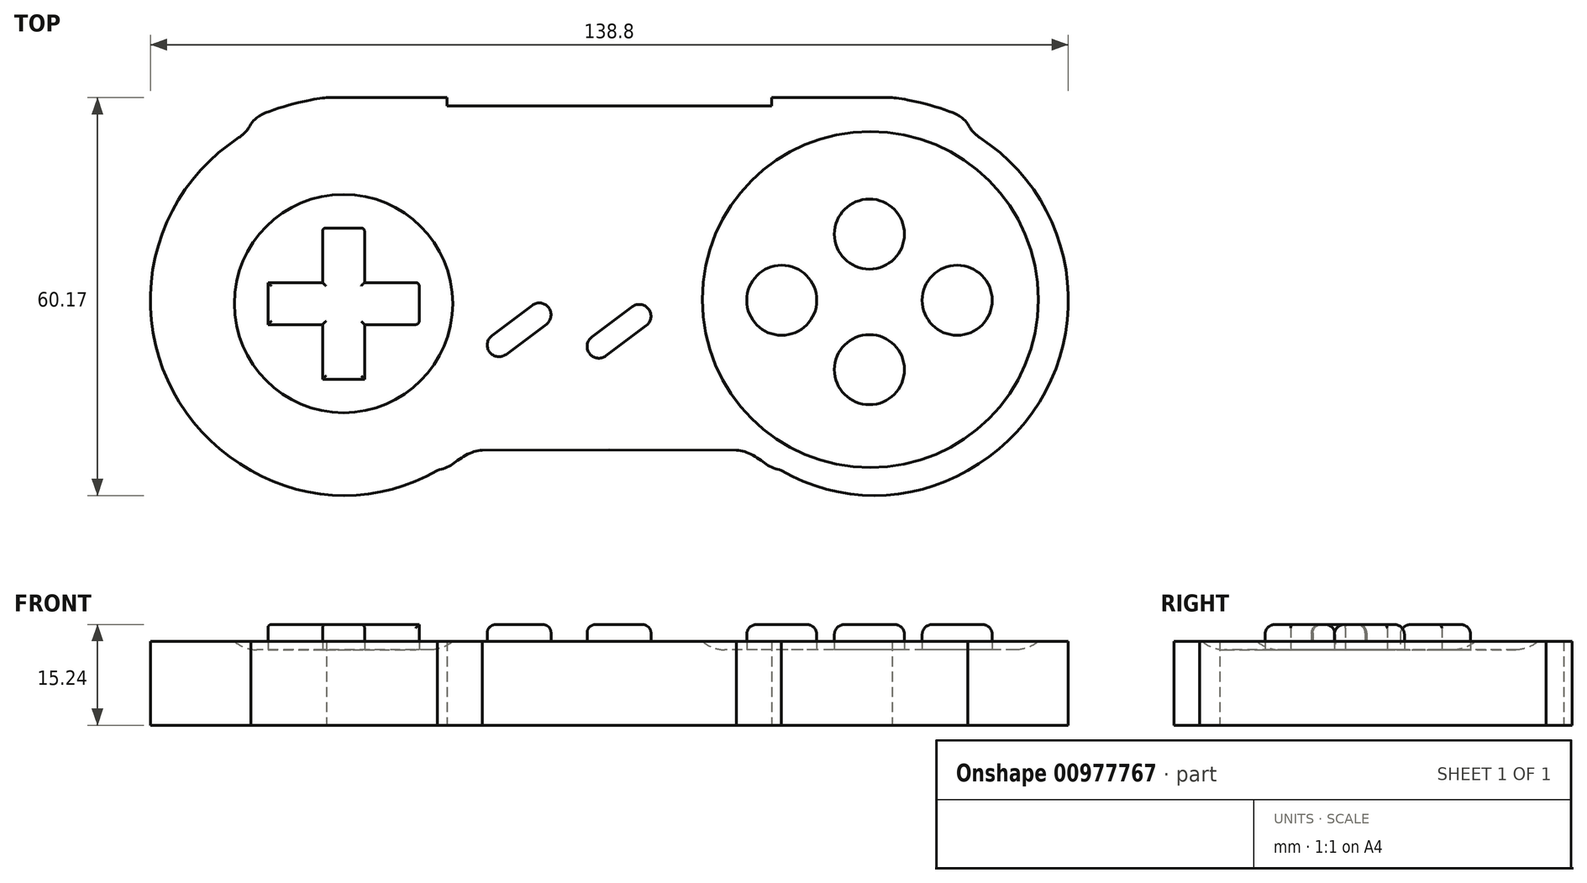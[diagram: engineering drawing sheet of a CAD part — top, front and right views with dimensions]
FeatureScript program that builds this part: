
annotation { "Feature Type Name" : "Feature", "Feature Type Description" : "" }
export const myFeature = defineFeature(function(context is Context, id is Id, definition is map)
    precondition{}
    {
        {
            var Q0;
            Q0=qCreatedBy(makeId("Top.planeOp"),FACE);
            var sketch = newSketch(context, id + "F0", { "sketchPlane" : qUnion([Q0])});
            skLineSegment(sketch, "E0.top", {"start": v(72.48, 34.93) * mm, "end": v(-72.48, 34.93) * mm});
            skLineSegment(sketch, "E0.left", {"start": v(72.48, -34.93) * mm, "end": v(72.48, 34.93) * mm});
            skLineSegment(sketch, "E0.right", {"start": v(-72.48, -34.93) * mm, "end": v(-72.48, 34.93) * mm});
            skPoint(sketch, "E0.middle", {"position": v(0, 0) * mm});
            skLineSegment(sketch, "E1", {"start": v(-72.48, -34.93) * mm, "end": v(72.48, -34.93) * mm});
            skLineSegment(sketch, "E2", {"start": v(0, 0) * mm, "end": v(0, 26.38) * mm});
            skLineSegment(sketch, "E3", {"start": v(0, 0) * mm, "end": v(0, -25.63) * mm});
            skLineSegment(sketch, "E4", {"start": v(0, 26.38) * mm, "end": v(-24.55, 26.38) * mm});
            skLineSegment(sketch, "E5", {"start": v(-24.55, 26.38) * mm, "end": v(-24.55, 27.65) * mm});
            skLineSegment(sketch, "E6", {"start": v(-24.55, 27.65) * mm, "end": v(-42.75, 27.65) * mm});
            skLineSegment(sketch, "E7", {"start": v(-54.18, 23.7) * mm, "end": v(-54.18, 22.7) * mm});
            skFitSpline(sketch, "E8", {"points": [v(-42.75, 27.65) * mm, v(-45.46, 27.23) * mm, v(-52.7, 25) * mm, v(-54.18, 23.7) * mm], "startDerivative": vector(-7.67, -0.85) * mm, "endDerivative": vector(-4.06, -5.33) * mm});
            skArc(sketch, "E9", {"start": v(-54.18, 22.7) * mm, "mid": v(-69.4, -3) * mm, "end": v(-54.18, -28.7) * mm});
            skArc(sketch, "E10", {"start": v(-54.18, -28.7) * mm, "mid": v(-40.08, -32.52) * mm, "end": v(-25.98, -28.7) * mm});
            skFitSpline(sketch, "E11", {"points": [v(-25.98, -28.7) * mm, v(-24.4, -28.18) * mm, v(-22.93, -27.2) * mm, v(-20.95, -26.07) * mm, v(-19.23, -25.65) * mm], "startDerivative": vector(6.95, 1.75) * mm, "endDerivative": vector(6.95, 1.14) * mm});
            skLineSegment(sketch, "E12", {"start": v(-19.23, -25.65) * mm, "end": v(0, -25.63) * mm});
            skLineSegment(sketch, "E13.MirrorCS", {"start": v(19.23, -25.65) * mm, "end": v(0, -25.63) * mm});
            skFitSpline(sketch, "E14.MirrorCS", {"points": [v(25.98, -28.7) * mm, v(24.4, -28.18) * mm, v(22.93, -27.2) * mm, v(20.95, -26.07) * mm, v(19.23, -25.65) * mm], "startDerivative": vector(-6.95, 1.75) * mm, "endDerivative": vector(-6.95, 1.14) * mm});
            skLineSegment(sketch, "E15.MirrorCS", {"start": v(0, 26.38) * mm, "end": v(24.55, 26.38) * mm});
            skLineSegment(sketch, "E16.MirrorCS", {"start": v(24.55, 27.65) * mm, "end": v(42.75, 27.65) * mm});
            skLineSegment(sketch, "E17.MirrorCS", {"start": v(24.55, 26.38) * mm, "end": v(24.55, 27.65) * mm});
            skFitSpline(sketch, "E18.MirrorCS", {"points": [v(42.75, 27.65) * mm, v(45.46, 27.23) * mm, v(52.7, 25) * mm, v(54.18, 23.7) * mm], "startDerivative": vector(7.67, -0.85) * mm, "endDerivative": vector(4.06, -5.33) * mm});
            skArc(sketch, "E19.MirrorCS", {"start": v(54.18, 22.7) * mm, "mid": v(69.4, -3) * mm, "end": v(54.18, -28.7) * mm});
            skLineSegment(sketch, "E20.MirrorCS", {"start": v(54.18, 23.7) * mm, "end": v(54.18, 22.7) * mm});
            skArc(sketch, "E21.MirrorCS", {"start": v(54.18, -28.7) * mm, "mid": v(40.08, -32.52) * mm, "end": v(25.98, -28.7) * mm});
            skSolve(sketch);
        }
        {
            var Q0;
            Q0=makeQuery(id+"F0.imprint","IMPRINT",FACE,{"disambiguationData":[TD([[makeQuery(id+"F0.imprint","IMPRINT",EDGE,{"derivedFrom":sQuery(id+"F0.wireOp",EDGE,"E2")}),1.0]])]});
            var Q1;
            Q1=makeQuery(id+"F0.imprint","IMPRINT",FACE,{"disambiguationData":[TD([[makeQuery(id+"F0.imprint","IMPRINT",EDGE,{"derivedFrom":sQuery(id+"F0.wireOp",EDGE,"E2")}),-1.0]])]});
            extrude(context, id + "F1", {"entities" : qUnion([Q0, Q1]), "depth" : 12.7 * mm, "offsetDistance" : 25.4 * mm});
        }
        {
            var Q0;
            Q0=makeQuery(id+"F1.opExtrude","CAP_FACE",FACE,{"disambiguationData":[OSD([sQuery(id+"F0.wireOp",EDGE,"E4"),sQuery(id+"F0.wireOp",EDGE,"E5"),sQuery(id+"F0.wireOp",EDGE,"E6"),sQuery(id+"F0.wireOp",EDGE,"E7"),sQuery(id+"F0.wireOp",EDGE,"E8"),sQuery(id+"F0.wireOp",EDGE,"E9"),sQuery(id+"F0.wireOp",EDGE,"E10"),sQuery(id+"F0.wireOp",EDGE,"E11"),sQuery(id+"F0.wireOp",EDGE,"E12"),sQuery(id+"F0.wireOp",EDGE,"E13.MirrorCS"),sQuery(id+"F0.wireOp",EDGE,"E14.MirrorCS"),sQuery(id+"F0.wireOp",EDGE,"E15.MirrorCS"),sQuery(id+"F0.wireOp",EDGE,"E16.MirrorCS"),sQuery(id+"F0.wireOp",EDGE,"E17.MirrorCS"),sQuery(id+"F0.wireOp",EDGE,"E18.MirrorCS"),sQuery(id+"F0.wireOp",EDGE,"E19.MirrorCS"),sQuery(id+"F0.wireOp",EDGE,"E20.MirrorCS"),sQuery(id+"F0.wireOp",EDGE,"E21.MirrorCS")])],"isStart":false});
            var sketch = newSketch(context, id + "F2", { "sketchPlane" : qUnion([Q0])});
            skLineSegment(sketch, "E22", {"start": v(-51.62, -3.49) * mm, "end": v(-51.62, -0.31) * mm});
            skLineSegment(sketch, "E23", {"start": v(-28.76, -3.49) * mm, "end": v(-28.76, -6.66) * mm});
            skLineSegment(sketch, "E24", {"start": v(-40.19, 7.94) * mm, "end": v(-43.36, 7.94) * mm});
            skLineSegment(sketch, "E25", {"start": v(-40.19, -14.92) * mm, "end": v(-37.01, -14.92) * mm});
            skLineSegment(sketch, "E26.bottom", {"start": v(-51.62, -0.31) * mm, "end": v(-43.36, -0.31) * mm});
            skLineSegment(sketch, "E26.top", {"start": v(-51.62, -6.66) * mm, "end": v(-43.36, -6.66) * mm});
            skLineSegment(sketch, "E26.left", {"start": v(-51.62, -0.31) * mm, "end": v(-51.62, -6.66) * mm});
            skLineSegment(sketch, "E26.right", {"start": v(-28.76, -0.31) * mm, "end": v(-28.76, -6.66) * mm});
            skLineSegment(sketch, "E27.bottom", {"start": v(-43.36, 7.94) * mm, "end": v(-37.01, 7.94) * mm});
            skLineSegment(sketch, "E27.top", {"start": v(-43.36, -14.92) * mm, "end": v(-37.01, -14.92) * mm});
            skLineSegment(sketch, "E27.left", {"start": v(-43.36, 7.94) * mm, "end": v(-43.36, -0.31) * mm});
            skLineSegment(sketch, "E27.right", {"start": v(-37.01, 7.94) * mm, "end": v(-37.01, -0.31) * mm});
            skLineSegment(sketch, "E28.trimOffspring", {"start": v(-37.01, -6.66) * mm, "end": v(-37.01, -14.92) * mm});
            skLineSegment(sketch, "E29.trimOffspring", {"start": v(-37.01, -6.66) * mm, "end": v(-28.76, -6.66) * mm});
            skLineSegment(sketch, "E30.trimOffspring", {"start": v(-43.36, -6.66) * mm, "end": v(-43.36, -14.92) * mm});
            skLineSegment(sketch, "E31.trimOffspring", {"start": v(-37.01, -0.31) * mm, "end": v(-28.76, -0.31) * mm});
            skCircle(sketch, "E32", {"center": v(26.06, -3) * mm, "radius": 5.3 * mm});
            skPoint(sketch, "E32.first.point", {"position": v(26.05, 2.3) * mm});
            skPoint(sketch, "E32.second.point", {"position": v(22.23, -6.65) * mm});
            skPoint(sketch, "E32.third.point", {"position": v(30.44, -5.98) * mm});
            skCircle(sketch, "E33", {"center": v(52.6, -3) * mm, "radius": 5.3 * mm});
            skCircle(sketch, "E34", {"center": v(39.33, 7.01) * mm, "radius": 5.3 * mm});
            skCircle(sketch, "E35", {"center": v(39.33, -13.48) * mm, "radius": 5.3 * mm});
            skLineSegment(sketch, "E36", {"start": v(-2.65, -8.55) * mm, "end": v(3.45, -3.98) * mm});
            skLineSegment(sketch, "E37", {"start": v(5.58, -6.82) * mm, "end": v(-0.52, -11.4) * mm});
            skArc(sketch, "E38", {"start": v(5.58, -6.82) * mm, "mid": v(5.94, -4.33) * mm, "end": v(3.45, -3.98) * mm});
            skArc(sketch, "E39", {"start": v(-2.65, -8.55) * mm, "mid": v(-3, -11.04) * mm, "end": v(-0.52, -11.4) * mm});
            skLineSegment(sketch, "E40", {"start": v(-17.75, -8.33) * mm, "end": v(-11.65, -3.76) * mm});
            skLineSegment(sketch, "E41", {"start": v(-9.52, -6.6) * mm, "end": v(-15.62, -11.17) * mm});
            skArc(sketch, "E42", {"start": v(-9.52, -6.6) * mm, "mid": v(-9.16, -4.11) * mm, "end": v(-11.65, -3.76) * mm});
            skArc(sketch, "E43", {"start": v(-17.75, -8.33) * mm, "mid": v(-18.1, -10.82) * mm, "end": v(-15.62, -11.17) * mm});
            skSolve(sketch);
        }
        {
            var Q0;
            Q0=makeQuery(id+"F2.imprint","IMPRINT",FACE,{"disambiguationData":[TD([[makeQuery(id+"F2.imprint","IMPRINT",EDGE,{"derivedFrom":sQuery(id+"F2.wireOp",EDGE,"E22")}),-1.0]])]});
            var Q1;
            Q1=makeQuery(id+"F2.imprint","IMPRINT",FACE,{"disambiguationData":[TD([[makeQuery(id+"F2.imprint","IMPRINT",EDGE,{"derivedFrom":sQuery(id+"F2.wireOp",EDGE,"E40")}),-1.0]])]});
            var Q2;
            Q2=makeQuery(id+"F2.imprint","IMPRINT",FACE,{"disambiguationData":[TD([[makeQuery(id+"F2.imprint","IMPRINT",EDGE,{"derivedFrom":sQuery(id+"F2.wireOp",EDGE,"E36")}),-1.0]])]});
            var Q3;
            Q3=makeQuery(id+"F2.imprint","IMPRINT",FACE,{"disambiguationData":[TD([[makeQuery(id+"F2.imprint","IMPRINT",EDGE,{"derivedFrom":sQuery(id+"F2.wireOp",EDGE,"E32")}),1.0]])]});
            var Q4;
            Q4=makeQuery(id+"F2.imprint","IMPRINT",FACE,{"disambiguationData":[TD([[makeQuery(id+"F2.imprint","IMPRINT",EDGE,{"derivedFrom":sQuery(id+"F2.wireOp",EDGE,"E34")}),1.0]])]});
            var Q5;
            Q5=makeQuery(id+"F2.imprint","IMPRINT",FACE,{"disambiguationData":[TD([[makeQuery(id+"F2.imprint","IMPRINT",EDGE,{"derivedFrom":sQuery(id+"F2.wireOp",EDGE,"E33")}),1.0]])]});
            var Q6;
            Q6=makeQuery(id+"F2.imprint","IMPRINT",FACE,{"disambiguationData":[TD([[makeQuery(id+"F2.imprint","IMPRINT",EDGE,{"derivedFrom":sQuery(id+"F2.wireOp",EDGE,"E35")}),1.0]])]});
            extrude(context, id + "F3", {"entities" : qUnion([Q0, Q1, Q2, Q3, Q4, Q5, Q6]), "operationType" : NewBodyOperationType.ADD, "depth" : 2.54 * mm, "offsetDistance" : 25.4 * mm});
        }
        {
            var Q0;
            Q0=makeQuery(id+"F3.opExtrude","SWEPT_EDGE",EDGE,{"disambiguationData":[OSD([sQuery(id+"F2.wireOp",EDGE,"E24"),sQuery(id+"F2.wireOp",EDGE,"E27.left")])]});
            var Q1;
            Q1=makeQuery(id+"F3.opExtrude","CAP_EDGE",EDGE,{"disambiguationData":[OSD([sQuery(id+"F2.wireOp",EDGE,"E24"),sQuery(id+"F2.wireOp",EDGE,"E27.bottom")])],"isStart":false});
            var Q2;
            Q2=makeQuery(id+"F3.opExtrude","SWEPT_EDGE",EDGE,{"disambiguationData":[OSD([sQuery(id+"F2.wireOp",EDGE,"E27.bottom"),sQuery(id+"F2.wireOp",EDGE,"E27.right")])]});
            var Q3;
            Q3=makeQuery(id+"F3.opExtrude","CAP_EDGE",EDGE,{"disambiguationData":[OSD([sQuery(id+"F2.wireOp",EDGE,"E27.right")])],"isStart":false});
            var Q4;
            Q4=makeQuery(id+"F3.opExtrude","CAP_EDGE",EDGE,{"disambiguationData":[OSD([sQuery(id+"F2.wireOp",EDGE,"E31.trimOffspring")])],"isStart":false});
            var Q5;
            Q5=makeQuery(id+"F3.opExtrude","SWEPT_EDGE",EDGE,{"disambiguationData":[OSD([sQuery(id+"F2.wireOp",EDGE,"E26.right"),sQuery(id+"F2.wireOp",EDGE,"E31.trimOffspring")])]});
            var Q6;
            Q6=makeQuery(id+"F3.opExtrude","SWEPT_EDGE",EDGE,{"disambiguationData":[OSD([sQuery(id+"F2.wireOp",EDGE,"E23"),sQuery(id+"F2.wireOp",EDGE,"E29.trimOffspring")])]});
            var Q7;
            Q7=makeQuery(id+"F3.opExtrude","CAP_EDGE",EDGE,{"disambiguationData":[OSD([sQuery(id+"F2.wireOp",EDGE,"E29.trimOffspring")])],"isStart":false});
            var Q8;
            Q8=makeQuery(id+"F3.opExtrude","CAP_EDGE",EDGE,{"disambiguationData":[OSD([sQuery(id+"F2.wireOp",EDGE,"E26.top")])],"isStart":false});
            var Q9;
            Q9=makeQuery(id+"F3.opExtrude","CAP_EDGE",EDGE,{"disambiguationData":[OSD([sQuery(id+"F2.wireOp",EDGE,"E26.bottom")])],"isStart":false});
            var Q10;
            Q10=makeQuery(id+"F3.opExtrude","CAP_EDGE",EDGE,{"disambiguationData":[OSD([sQuery(id+"F2.wireOp",EDGE,"E27.left")])],"isStart":false});
            var Q11;
            Q11=makeQuery(id+"F3.opExtrude","CAP_EDGE",EDGE,{"disambiguationData":[OSD([sQuery(id+"F2.wireOp",EDGE,"E22"),sQuery(id+"F2.wireOp",EDGE,"E26.left")])],"isStart":false});
            var Q12;
            Q12=makeQuery(id+"F3.opExtrude","CAP_EDGE",EDGE,{"disambiguationData":[OSD([sQuery(id+"F2.wireOp",EDGE,"E25"),sQuery(id+"F2.wireOp",EDGE,"E27.top")])],"isStart":false});
            var Q13;
            Q13=makeQuery(id+"F3.opExtrude","CAP_EDGE",EDGE,{"disambiguationData":[OSD([sQuery(id+"F2.wireOp",EDGE,"E30.trimOffspring")])],"isStart":false});
            var Q14;
            Q14=makeQuery(id+"F3.opExtrude","CAP_EDGE",EDGE,{"disambiguationData":[OSD([sQuery(id+"F2.wireOp",EDGE,"E28.trimOffspring")])],"isStart":false});
            fillet(context, id + "F4", {"entities" : qUnion([Q0, Q1, Q2, Q3, Q4, Q5, Q6, Q7, Q8, Q9, Q10, Q11, Q12, Q13, Q14]), "radius" : 0.5 * mm, "tangentPropagation" : true, "allowEdgeOverflow" : false});
        }
        {
            var Q0;
            Q0=makeQuery(id+"F3.opExtrude","CAP_EDGE",EDGE,{"disambiguationData":[OSD([sQuery(id+"F2.wireOp",EDGE,"E40")])],"isStart":false});
            var Q1;
            Q1=makeQuery(id+"F3.opExtrude","CAP_EDGE",EDGE,{"disambiguationData":[OSD([sQuery(id+"F2.wireOp",EDGE,"E36")])],"isStart":false});
            fillet(context, id + "F5", {"entities" : qUnion([Q0, Q1]), "radius" : 1.27 * mm, "tangentPropagation" : true, "allowEdgeOverflow" : false});
        }
        {
            var Q0;
            Q0=makeQuery(id+"F3.opExtrude","CAP_EDGE",EDGE,{"disambiguationData":[OSD([sQuery(id+"F2.wireOp",EDGE,"E32")])],"isStart":false});
            var Q1;
            Q1=makeQuery(id+"F3.opExtrude","CAP_EDGE",EDGE,{"disambiguationData":[OSD([sQuery(id+"F2.wireOp",EDGE,"E33")])],"isStart":false});
            var Q2;
            Q2=makeQuery(id+"F3.opExtrude","CAP_EDGE",EDGE,{"disambiguationData":[OSD([sQuery(id+"F2.wireOp",EDGE,"E34")])],"isStart":false});
            var Q3;
            Q3=makeQuery(id+"F3.opExtrude","CAP_EDGE",EDGE,{"disambiguationData":[OSD([sQuery(id+"F2.wireOp",EDGE,"E35")])],"isStart":false});
            fillet(context, id + "F6", {"entities" : qUnion([Q0, Q1, Q2, Q3]), "radius" : 1.52 * mm, "tangentPropagation" : true, "allowEdgeOverflow" : false});
        }
        {
            var Q0;
            Q0=makeQuery(id+"F1.opExtrude","CAP_FACE",FACE,{"disambiguationData":[OSD([sQuery(id+"F0.wireOp",EDGE,"E4"),sQuery(id+"F0.wireOp",EDGE,"E5"),sQuery(id+"F0.wireOp",EDGE,"E6"),sQuery(id+"F0.wireOp",EDGE,"E7"),sQuery(id+"F0.wireOp",EDGE,"E8"),sQuery(id+"F0.wireOp",EDGE,"E9"),sQuery(id+"F0.wireOp",EDGE,"E10"),sQuery(id+"F0.wireOp",EDGE,"E11"),sQuery(id+"F0.wireOp",EDGE,"E12"),sQuery(id+"F0.wireOp",EDGE,"E13.MirrorCS"),sQuery(id+"F0.wireOp",EDGE,"E14.MirrorCS"),sQuery(id+"F0.wireOp",EDGE,"E15.MirrorCS"),sQuery(id+"F0.wireOp",EDGE,"E16.MirrorCS"),sQuery(id+"F0.wireOp",EDGE,"E17.MirrorCS"),sQuery(id+"F0.wireOp",EDGE,"E18.MirrorCS"),sQuery(id+"F0.wireOp",EDGE,"E19.MirrorCS"),sQuery(id+"F0.wireOp",EDGE,"E20.MirrorCS"),sQuery(id+"F0.wireOp",EDGE,"E21.MirrorCS")])],"isStart":false});
            var sketch = newSketch(context, id + "F7", { "sketchPlane" : qUnion([Q0])});
            skPoint(sketch, "E44", {"position": v(-51.11, -3.49) * mm});
            skPoint(sketch, "E45", {"position": v(-40.19, 7.43) * mm});
            skCircle(sketch, "E46", {"center": v(-40.19, -3.49) * mm, "radius": 16.51 * mm});
            skCircle(sketch, "E47", {"center": v(39.46, -2.89) * mm, "radius": 25.4 * mm});
            skSolve(sketch);
        }
        {
            var Q0;
            Q0=makeQuery(id+"F7.imprint","IMPRINT",FACE,{"disambiguationData":[TD([[makeQuery(id+"F7.imprint","IMPRINT",EDGE,{"derivedFrom":sQuery(id+"F7.wireOp",EDGE,"E46")}),1.0]])]});
            var Q1;
            Q1=makeQuery(id+"F7.imprint","IMPRINT",FACE,{"disambiguationData":[TD([[makeQuery(id+"F7.imprint","IMPRINT",EDGE,{"derivedFrom":sQuery(id+"F7.wireOp",EDGE,"E47")}),1.0]])]});
            extrude(context, id + "F8", {"entities" : qUnion([Q0, Q1]), "operationType" : NewBodyOperationType.REMOVE, "oppositeDirection" : true, "depth" : 1.27 * mm, "offsetDistance" : 25.4 * mm});
        }
        {
            var Q0;
            Q0=makeQuery(id+"F1.opExtrude","SWEPT_EDGE",EDGE,{"disambiguationData":[OSD([sQuery(id+"F0.wireOp",EDGE,"E7"),sQuery(id+"F0.wireOp",EDGE,"E9")])]});
            fillet(context, id + "F9", {"entities" : qUnion([Q0]), "radius" : 5.08 * mm, "tangentPropagation" : true, "allowEdgeOverflow" : false});
        }
        {
            var Q0;
            Q0=makeQuery(id+"F1.opExtrude","SWEPT_EDGE",EDGE,{"disambiguationData":[OSD([sQuery(id+"F0.wireOp",EDGE,"E19.MirrorCS"),sQuery(id+"F0.wireOp",EDGE,"E20.MirrorCS")])]});
            fillet(context, id + "F10", {"entities" : qUnion([Q0]), "radius" : 5.08 * mm, "tangentPropagation" : true, "allowEdgeOverflow" : false});
        }
        {
            var Q0;
            Q0=makeQuery(id+"F8.boolean.opBoolean","COPY",EDGE,{"derivedFrom":makeQuery(id+"F8.opExtrude","CAP_EDGE",EDGE,{"disambiguationData":[OSD([sQuery(id+"F7.wireOp",EDGE,"E47")])],"isStart":false})});
            var Q1;
            Q1=makeQuery(id+"F8.boolean.opBoolean","COPY",EDGE,{"derivedFrom":makeQuery(id+"F8.opExtrude","CAP_EDGE",EDGE,{"disambiguationData":[OSD([sQuery(id+"F7.wireOp",EDGE,"E46")])],"isStart":false})});
            fillet(context, id + "F11", {"entities" : qUnion([Q0, Q1]), "radius" : 5.08 * mm, "tangentPropagation" : true, "allowEdgeOverflow" : false});
        }
    });
